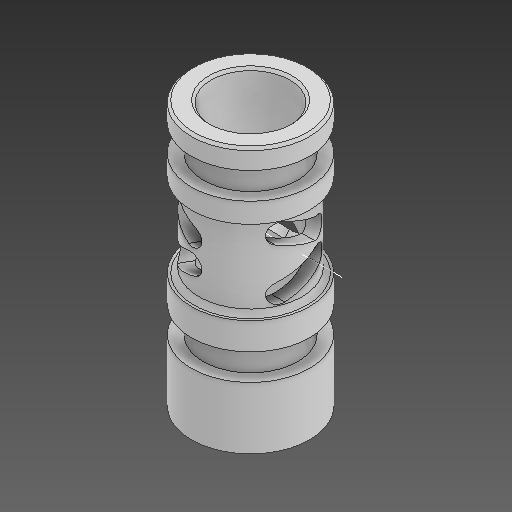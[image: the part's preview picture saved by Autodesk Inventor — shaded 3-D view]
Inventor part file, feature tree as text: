
AUTODESK INVENTOR PART (.ipt)
format: ipt  version: 2021 (Build 250183000, 183)  size: 301,056 bytes
history: native  units: in
note: dims shown in document units (in); Inventor stores cm internally (conversion verified against a paired STEP export)
features: other x7, sketch x5, plane x1
ambient origin geometry x8: Origin, YZ Plane, XZ Plane, XY Plane, X Axis, Y Axis, Z Axis, Center Point
bodies: Solid1 (feature_tree)
feature tree (13):
  other  "outer_sleeve.ipt"
  other  "Solid1::outer_sleeve.ipt"
  other  "TaggingFeature1"
  sketch  "Sketch2"  dims[d0=0.3937in]
  sketch  "Sketch3"
  sketch  "Sketch4"
  sketch  "Sketch5"
  sketch  "Sketch10"
  plane  "Work Plane1"
  other  "Work Axis1"
  other  "Work Axis2"
  other  "Srf1"
  other  "Srf1::Derived"
